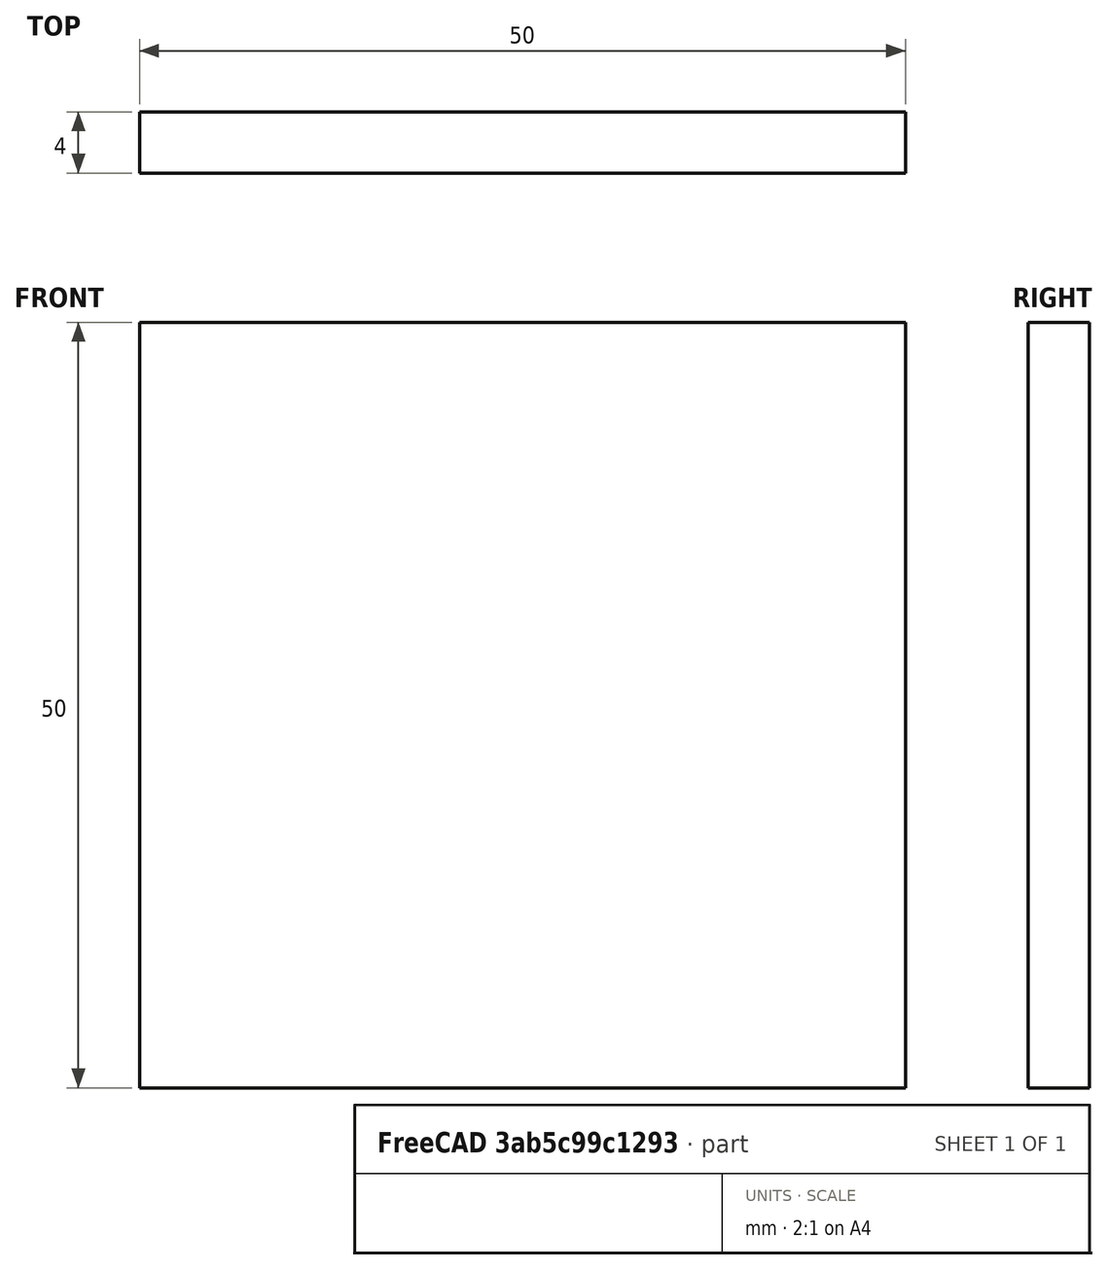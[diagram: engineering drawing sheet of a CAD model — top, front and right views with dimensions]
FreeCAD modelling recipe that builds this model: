
FCSTD DOCUMENT  (FreeCAD 0.15R4671 (Git))
Label: Flat Bar 50x4 EN10058 S235JR
License: All rights reserved
LicenseURL: http://en.wikipedia.org/wiki/All_rights_reserved
objects: Sketcher::SketchObject×1, Part::Extrusion×1
note: 2 computed .brp shape members not serialized (recipe doc carries the construction recipe); baked Part::Feature solids carry a one-line shape summary decoded from their .brp

FEATURE [Sketcher::SketchObject] Sketch
  sketch-geometry (4):
    g0: LineSegment StartX=-25 StartY=-2 StartZ=0 EndX=25 EndY=-2 EndZ=0
    g1: LineSegment StartX=25 StartY=-2 StartZ=0 EndX=25 EndY=2 EndZ=0
    g2: LineSegment StartX=25 StartY=2 StartZ=0 EndX=-25 EndY=2 EndZ=0
    g3: LineSegment StartX=-25 StartY=2 StartZ=0 EndX=-25 EndY=-2 EndZ=0
  constraints (12):
    c: Coincident(g0,g1)
    c: Coincident(g1,g2)
    c: Coincident(g2,g3)
    c: Coincident(g3,g0)
    c: Horizontal(g0)
    c: Horizontal(g2)
    c: Vertical(g1)
    c: Vertical(g3)
    c: Symmetric(g1,g2,g-2)
    c: Symmetric(g0,g1,g-1)
    c: DistanceY(g1) = 4
    c: DistanceX(g0) = 50
FEATURE [Part::Extrusion] Extrude  label="Flat Bar 50x4 EN10058 S235JR"
  Base = -> Sketch
  Dir = (0,0,50)
  Solid = true
